# Revit family: CRB-10-E
name_source: partatom
category: Mechanical Equipment
revit_build: Autodesk Revit 2015 (Build: 20140606_1530(x64)
units: mm (PartAtom-declared; Revit-internal decimal feet)

## types (11) — shared parameters
Depth = 0' - 5 3/16"
Description = Constant Volume Regulator for Exhaust or Return Applications
Keynote = Arrangement #1 shown, consult factory for other arrangement model options.
Manufacturer = United Enertech Corporation
Model = CRB-10-E
URL = http://unitedenertech.com

## per-type parameters (varying)
| type | Box Height | Box Width | CR Model | Hole Radius |
| 6 x 4 (4" Damper) | 0' - 4" | 0' - 6" | CR 4 (Sleeveless) | 0' - 1 3/4" |
| 6 x 6 (4" Damper) | 0' - 6" | 0' - 6" | CR 4 (Sleeveless) | 0' - 1 3/4" |
| 6 x 6 (5" Damper) | 0' - 6" | 0' - 6" | CR 5 (Sleeveless) | 0' - 2 7/32" |
| 8 x 8 (4" Damper) | 0' - 8" | 0' - 8" | CR 4 (Sleeveless) | 0' - 1 3/4" |
| 8 x 8 (5" Damper) | 0' - 8" | 0' - 8" | CR 5 (Sleeveless) | 0' - 2 7/32" |
| 8 x 8 (6" Damper) | 0' - 8" | 0' - 8" | CR 6 (Sleeveless) | 0' - 2 7/8" |
| 10 x 10 (6" Damper) | 0' - 10" | 0' - 10" | CR 6 (Sleeveless) | 0' - 2 7/8" |
| 10 x 10 (8" Damper) | 0' - 10" | 0' - 10" | CR 8 (Sleeveless) | 0' - 3 3/4" |
| 12 x 12 (8" Damper) | 1' - 0" | 1' - 0" | CR 8 (Sleeveless) | 0' - 3 3/4" |
| 12 x 12 (10" Damper) | 1' - 0" | 1' - 0" | CR 10 (Sleeveless) | 0' - 4 3/4" |
| 14 x 14 (10" Damper) | 1' - 2" | 1' - 2" | CR 10 (Sleeveless) | 0' - 4 3/4" |

## geometry (parser evidence)
native form markers: Sweep x13
no freeform markers — native parametric forms only
